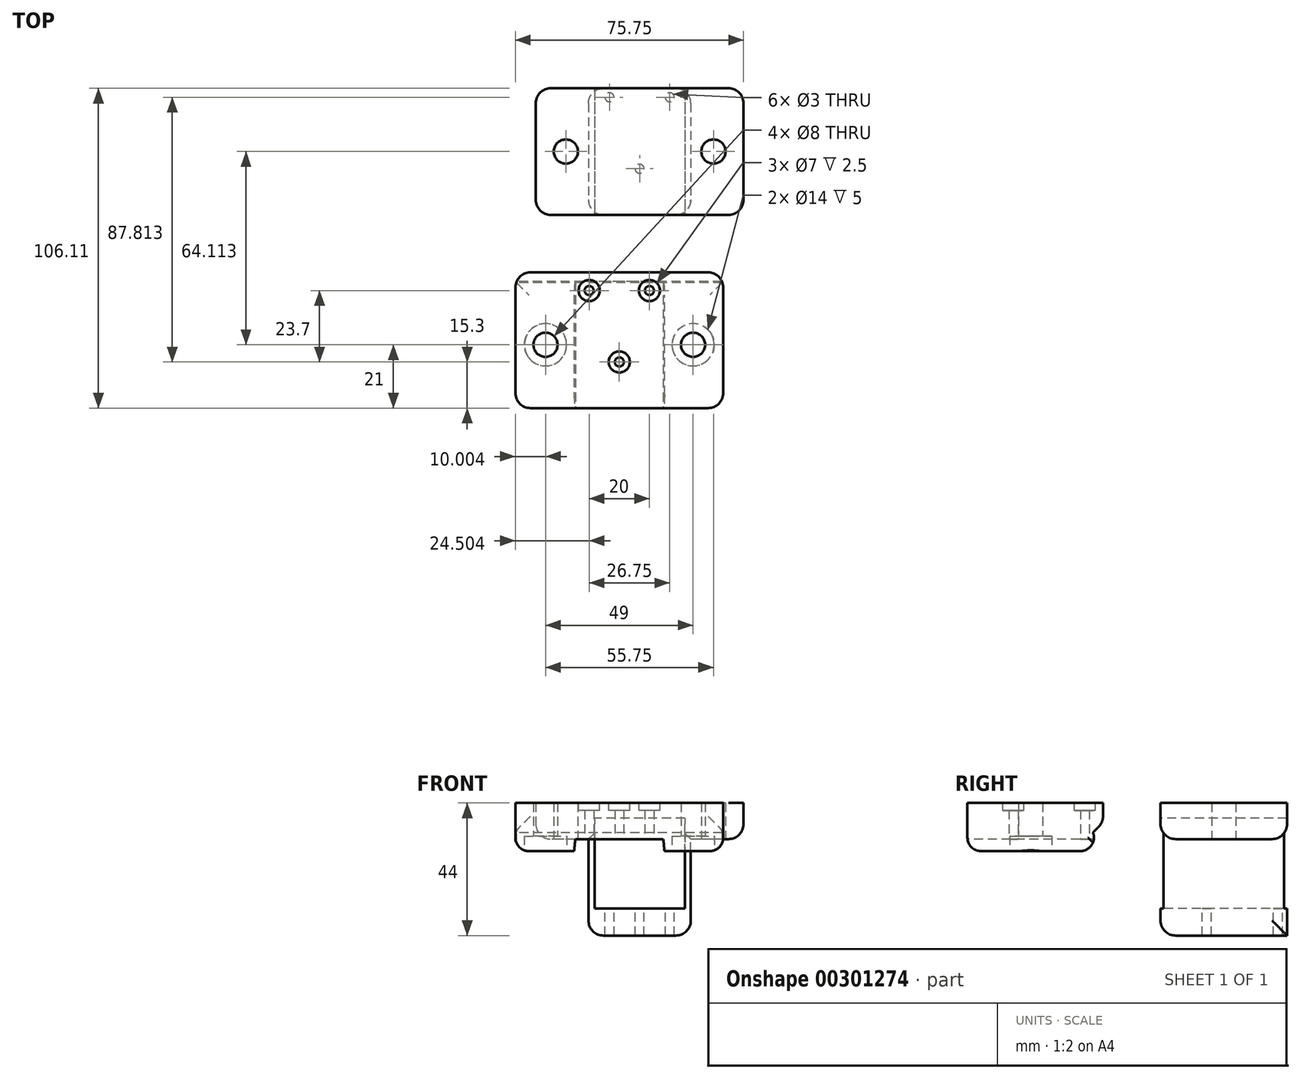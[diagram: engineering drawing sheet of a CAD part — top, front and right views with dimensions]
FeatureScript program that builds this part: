
annotation { "Feature Type Name" : "Feature", "Feature Type Description" : "" }
export const myFeature = defineFeature(function(context is Context, id is Id, definition is map)
    precondition{}
    {
        {
            var Q0;
            Q0=qCreatedBy(makeId("Top.planeOp"),FACE);
            var sketch = newSketch(context, id + "F0", { "sketchPlane" : qUnion([Q0])});
            skLineSegment(sketch, "E0.bottom", {"start": v(-79.38, 0) * mm, "end": v(-10.38, 0) * mm});
            skLineSegment(sketch, "E0.top", {"start": v(-79.38, -42) * mm, "end": v(-10.38, -42) * mm});
            skLineSegment(sketch, "E0.left", {"start": v(-79.38, 0) * mm, "end": v(-79.38, -42) * mm});
            skLineSegment(sketch, "E0.right", {"start": v(-10.38, 0) * mm, "end": v(-10.38, -42) * mm});
            skPoint(sketch, "E1", {"position": v(-59.38, 0) * mm});
            skLineSegment(sketch, "E2", {"start": v(-59.38, 0) * mm, "end": v(-59.38, -42) * mm});
            skPoint(sketch, "E3", {"position": v(-30.38, 0) * mm});
            skLineSegment(sketch, "E4", {"start": v(-30.38, 0) * mm, "end": v(-30.38, -42) * mm});
            skLineSegment(sketch, "E5", {"start": v(-44.88, 0) * mm, "end": v(-44.88, -42) * mm});
            skLineSegment(sketch, "E6", {"start": v(-59.38, -3) * mm, "end": v(-30.38, -3) * mm});
            skPoint(sketch, "E7", {"position": v(-44.88, -3) * mm});
            skPoint(sketch, "E8", {"position": v(-54.88, -3) * mm});
            skPoint(sketch, "E9", {"position": v(-34.88, -3) * mm});
            skPoint(sketch, "E10", {"position": v(-44.88, -26.7) * mm});
            skCircle(sketch, "E11", {"center": v(-54.88, -3) * mm, "radius": 1.5 * mm});
            skCircle(sketch, "E12", {"center": v(-34.88, -3) * mm, "radius": 1.5 * mm});
            skCircle(sketch, "E13", {"center": v(-44.88, -26.7) * mm, "radius": 1.5 * mm});
            skPoint(sketch, "E14", {"position": v(-20.38, -42) * mm});
            skLineSegment(sketch, "E15", {"start": v(-20.38, -42) * mm, "end": v(-20.38, 0) * mm});
            skPoint(sketch, "E16", {"position": v(-20.38, -21) * mm});
            skCircle(sketch, "E17", {"center": v(-20.38, -21) * mm, "radius": 4 * mm});
            skPoint(sketch, "E18", {"position": v(-69.38, -42) * mm});
            skLineSegment(sketch, "E19", {"start": v(-69.38, -42) * mm, "end": v(-69.38, 0) * mm});
            skPoint(sketch, "E20", {"position": v(-69.38, -21) * mm});
            skCircle(sketch, "E21", {"center": v(-69.38, -21) * mm, "radius": 4 * mm});
            skSolve(sketch);
        }
        {
            var Q0;
            {var subQ5=sQuery(id+"F0.wireOp",EDGE,"E0.right");Q0=makeQuery(id+"F0.imprint","IMPRINT",FACE,{"disambiguationData":[TD([[makeQuery(id+"F0.imprint","IMPRINT",EDGE,{"derivedFrom":subQ5}),-1.0]])]});}
            var Q1;
            {var subQ0=sQuery(id+"F0.wireOp",EDGE,"E4");var subQ4=sQuery(id+"F0.wireOp",EDGE,"E0.bottom");var subQ5=makeQuery(id+"F0.imprint","INTERSECT",VERTEX,{"derivedFrom":[subQ4,subQ0]});Q1=makeQuery(id+"F0.imprint","IMPRINT",FACE,{"disambiguationData":[TD([[makeQuery(id+"F0.imprint","IMPRINT",EDGE,{"disambiguationData":[TD([[subQ5,-1.0]])],"derivedFrom":subQ4}),-1.0]])]});}
            var Q2;
            {var subQ1=sQuery(id+"F0.wireOp",EDGE,"E0.top");var subQ5=sQuery(id+"F0.wireOp",EDGE,"E4");var subQ6=makeQuery(id+"F0.imprint","INTERSECT",VERTEX,{"derivedFrom":[subQ1,subQ5]});Q2=makeQuery(id+"F0.imprint","IMPRINT",FACE,{"disambiguationData":[TD([[makeQuery(id+"F0.imprint","IMPRINT",EDGE,{"disambiguationData":[TD([[subQ6,1.0]])],"derivedFrom":subQ1}),1.0]])]});}
            var Q3;
            {var subQ1=sQuery(id+"F0.wireOp",EDGE,"E0.top");var subQ8=sQuery(id+"F0.wireOp",EDGE,"E2");var subQ9=makeQuery(id+"F0.imprint","INTERSECT",VERTEX,{"derivedFrom":[subQ1,subQ8]});Q3=makeQuery(id+"F0.imprint","IMPRINT",FACE,{"disambiguationData":[TD([[makeQuery(id+"F0.imprint","IMPRINT",EDGE,{"disambiguationData":[TD([[subQ9,-1.0]])],"derivedFrom":subQ1}),1.0]])]});}
            var Q4;
            {var subQ0=sQuery(id+"F0.wireOp",EDGE,"E2");var subQ4=sQuery(id+"F0.wireOp",EDGE,"E0.bottom");var subQ5=makeQuery(id+"F0.imprint","INTERSECT",VERTEX,{"derivedFrom":[subQ4,subQ0]});Q4=makeQuery(id+"F0.imprint","IMPRINT",FACE,{"disambiguationData":[TD([[makeQuery(id+"F0.imprint","IMPRINT",EDGE,{"disambiguationData":[TD([[subQ5,1.0]])],"derivedFrom":subQ4}),-1.0]])]});}
            var Q5;
            {var subQ5=sQuery(id+"F0.wireOp",EDGE,"E0.left");Q5=makeQuery(id+"F0.imprint","IMPRINT",FACE,{"disambiguationData":[TD([[makeQuery(id+"F0.imprint","IMPRINT",EDGE,{"derivedFrom":subQ5}),1.0]])]});}
            var Q6;
            {var subQ1=sQuery(id+"F0.wireOp",EDGE,"E0.bottom");var subQ5=sQuery(id+"F0.wireOp",EDGE,"E2");var subQ6=makeQuery(id+"F0.imprint","INTERSECT",VERTEX,{"derivedFrom":[subQ1,subQ5]});Q6=makeQuery(id+"F0.imprint","IMPRINT",FACE,{"disambiguationData":[TD([[makeQuery(id+"F0.imprint","IMPRINT",EDGE,{"disambiguationData":[TD([[subQ6,-1.0]])],"derivedFrom":subQ1}),-1.0]])]});}
            var Q7;
            {var subQ5=sQuery(id+"F0.wireOp",EDGE,"E4");var subQ6=sQuery(id+"F0.wireOp",EDGE,"E0.bottom");var subQ7=makeQuery(id+"F0.imprint","INTERSECT",VERTEX,{"derivedFrom":[subQ6,subQ5]});Q7=makeQuery(id+"F0.imprint","IMPRINT",FACE,{"disambiguationData":[TD([[makeQuery(id+"F0.imprint","IMPRINT",EDGE,{"disambiguationData":[TD([[subQ7,1.0]])],"derivedFrom":subQ6}),-1.0]])]});}
            extrude(context, id + "F1", {"entities" : qUnion([Q0, Q1, Q2, Q3, Q4, Q5, Q6, Q7]), "depth" : 12 * mm});
        }
        {
            var Q0;
            {var subQ5=sQuery(id+"F0.wireOp",EDGE,"E0.right");Q0=makeQuery(id+"F0.imprint","IMPRINT",FACE,{"disambiguationData":[TD([[makeQuery(id+"F0.imprint","IMPRINT",EDGE,{"derivedFrom":subQ5}),-1.0]])]});}
            var Q1;
            {var subQ0=sQuery(id+"F0.wireOp",EDGE,"E4");var subQ4=sQuery(id+"F0.wireOp",EDGE,"E0.bottom");var subQ5=makeQuery(id+"F0.imprint","INTERSECT",VERTEX,{"derivedFrom":[subQ4,subQ0]});Q1=makeQuery(id+"F0.imprint","IMPRINT",FACE,{"disambiguationData":[TD([[makeQuery(id+"F0.imprint","IMPRINT",EDGE,{"disambiguationData":[TD([[subQ5,-1.0]])],"derivedFrom":subQ4}),-1.0]])]});}
            var Q2;
            {var subQ0=sQuery(id+"F0.wireOp",EDGE,"E2");var subQ4=sQuery(id+"F0.wireOp",EDGE,"E0.bottom");var subQ5=makeQuery(id+"F0.imprint","INTERSECT",VERTEX,{"derivedFrom":[subQ4,subQ0]});Q2=makeQuery(id+"F0.imprint","IMPRINT",FACE,{"disambiguationData":[TD([[makeQuery(id+"F0.imprint","IMPRINT",EDGE,{"disambiguationData":[TD([[subQ5,1.0]])],"derivedFrom":subQ4}),-1.0]])]});}
            var Q3;
            {var subQ5=sQuery(id+"F0.wireOp",EDGE,"E0.left");Q3=makeQuery(id+"F0.imprint","IMPRINT",FACE,{"disambiguationData":[TD([[makeQuery(id+"F0.imprint","IMPRINT",EDGE,{"derivedFrom":subQ5}),1.0]])]});}
            extrude(context, id + "F2", {"entities" : qUnion([Q0, Q1, Q2, Q3]), "operationType" : NewBodyOperationType.ADD, "oppositeDirection" : true, "depth" : 4 * mm});
        }
        {
            var Q0;
            Q0=makeQuery(id+"F2.opExtrude","CAP_EDGE",EDGE,{"disambiguationData":[OSD([sQuery(id+"F0.wireOp",EDGE,"E2")])],"isStart":false});
            chamfer(context, id + "F3", {"entities" : qUnion([Q0]), "chamferType" : ChamferType.TWO_OFFSETS, "width1" : 0.5 * mm, "oppositeDirection" : false, "width2" : 5 * mm, "tangentPropagation" : true});
        }
        {
            var Q0;
            Q0=makeQuery(id+"F2.opExtrude","CAP_EDGE",EDGE,{"disambiguationData":[OSD([sQuery(id+"F0.wireOp",EDGE,"E4")])],"isStart":false});
            chamfer(context, id + "F4", {"entities" : qUnion([Q0]), "chamferType" : ChamferType.TWO_OFFSETS, "width1" : 5 * mm, "oppositeDirection" : false, "width2" : 0.5 * mm, "tangentPropagation" : true});
        }
        {
            var Q0;
            Q0=makeQuery(id+"F2.opExtrude","CAP_FACE",FACE,{"disambiguationData":[OSD([sQuery(id+"F0.wireOp",EDGE,"E0.bottom"),sQuery(id+"F0.wireOp",EDGE,"E0.top"),sQuery(id+"F0.wireOp",EDGE,"E0.right"),sQuery(id+"F0.wireOp",EDGE,"E4"),sQuery(id+"F0.wireOp",EDGE,"E17")])],"isStart":false});
            var sketch = newSketch(context, id + "F5", { "sketchPlane" : qUnion([Q0])});
            skCircle(sketch, "E22", {"center": v(-20.38, 21) * mm, "radius": 7 * mm});
            skSolve(sketch);
        }
        {
            var Q0;
            Q0=makeQuery(id+"F5.imprint","IMPRINT",FACE,{"disambiguationData":[TD([[makeQuery(id+"F5.imprint","IMPRINT",EDGE,{"derivedFrom":sQuery(id+"F5.wireOp",EDGE,"E22")}),1.0]])]});
            extrude(context, id + "F6", {"entities" : qUnion([Q0]), "operationType" : NewBodyOperationType.REMOVE, "oppositeDirection" : true, "depth" : 5 * mm});
        }
        {
            var Q0;
            Q0=makeQuery(id+"F2.opExtrude","CAP_FACE",FACE,{"disambiguationData":[OSD([sQuery(id+"F0.wireOp",EDGE,"E0.bottom"),sQuery(id+"F0.wireOp",EDGE,"E0.top"),sQuery(id+"F0.wireOp",EDGE,"E0.left"),sQuery(id+"F0.wireOp",EDGE,"E2"),sQuery(id+"F0.wireOp",EDGE,"E21")])],"isStart":false});
            var sketch = newSketch(context, id + "F7", { "sketchPlane" : qUnion([Q0])});
            skCircle(sketch, "E23", {"center": v(-69.38, 21) * mm, "radius": 7 * mm});
            skSolve(sketch);
        }
        {
            var Q0;
            Q0=makeQuery(id+"F7.imprint","IMPRINT",FACE,{"disambiguationData":[TD([[makeQuery(id+"F7.imprint","IMPRINT",EDGE,{"derivedFrom":sQuery(id+"F7.wireOp",EDGE,"E23")}),1.0]])]});
            extrude(context, id + "F8", {"entities" : qUnion([Q0]), "operationType" : NewBodyOperationType.REMOVE, "oppositeDirection" : true, "depth" : 5 * mm});
        }
        {
            var Q0;
            Q0=makeQuery(id+"F2.opExtrude","CAP_EDGE",EDGE,{"disambiguationData":[OSD([sQuery(id+"F0.wireOp",EDGE,"E0.right")])],"isStart":false});
            var Q1;
            Q1=makeQuery(id+"F2.opExtrude","CAP_EDGE",EDGE,{"disambiguationData":[OSD([sQuery(id+"F0.wireOp",EDGE,"E0.left")])],"isStart":false});
            var Q2;
            {var subQ0=sQuery(id+"F0.wireOp",EDGE,"E0.top");Q2=makeQuery(id+"F2.opExtrude","CAP_EDGE",EDGE,{"disambiguationData":[OSD([subQ0]),TDD([makeQuery(id+"F0.imprint","IMPRINT",EDGE,{"disambiguationData":[TD([[makeQuery(id+"F0.imprint","INTERSECT",VERTEX,{"derivedFrom":[subQ0,sQuery(id+"F0.wireOp",EDGE,"E0.left")]}),-1.0]])],"derivedFrom":subQ0}),makeQuery(id+"F0.imprint","IMPRINT",EDGE,{"disambiguationData":[TD([[makeQuery(id+"F0.imprint","INTERSECT",VERTEX,{"derivedFrom":[subQ0,sQuery(id+"F0.wireOp",EDGE,"E2")]}),1.0]])],"derivedFrom":subQ0})])],"isStart":false});}
            var Q3;
            {var subQ0=sQuery(id+"F0.wireOp",EDGE,"E0.bottom");Q3=makeQuery(id+"F2.opExtrude","CAP_EDGE",EDGE,{"disambiguationData":[OSD([subQ0]),TDD([makeQuery(id+"F0.imprint","IMPRINT",EDGE,{"disambiguationData":[TD([[makeQuery(id+"F0.imprint","INTERSECT",VERTEX,{"derivedFrom":[subQ0,sQuery(id+"F0.wireOp",EDGE,"E0.left")]}),-1.0]])],"derivedFrom":subQ0}),makeQuery(id+"F0.imprint","IMPRINT",EDGE,{"disambiguationData":[TD([[makeQuery(id+"F0.imprint","INTERSECT",VERTEX,{"derivedFrom":[subQ0,sQuery(id+"F0.wireOp",EDGE,"E2")]}),1.0]])],"derivedFrom":subQ0})])],"isStart":false});}
            fillet(context, id + "F9", {"entities" : qUnion([Q0, Q1, Q2, Q3]), "radius" : 4.5 * mm, "allowEdgeOverflow" : false});
        }
        {
            var Q0;
            {var subQ0=sQuery(id+"F0.wireOp",EDGE,"E0.bottom");Q0=makeQuery(id+"F2.boolean.opBoolean","MERGE",FACE,{"derivedFrom":[makeQuery(id+"F1.opExtrude","SWEPT_FACE",FACE,{"disambiguationData":[OSD([subQ0])]}),makeQuery(id+"F2.opExtrude","SWEPT_FACE",FACE,{"disambiguationData":[OSD([subQ0]),TDD([makeQuery(id+"F0.imprint","IMPRINT",EDGE,{"disambiguationData":[TD([[makeQuery(id+"F0.imprint","INTERSECT",VERTEX,{"derivedFrom":[subQ0,sQuery(id+"F0.wireOp",EDGE,"E0.left")]}),-1.0]])],"derivedFrom":subQ0}),makeQuery(id+"F0.imprint","IMPRINT",EDGE,{"disambiguationData":[TD([[makeQuery(id+"F0.imprint","INTERSECT",VERTEX,{"derivedFrom":[subQ0,sQuery(id+"F0.wireOp",EDGE,"E2")]}),1.0]])],"derivedFrom":subQ0})])]}),makeQuery(id+"F2.opExtrude","SWEPT_FACE",FACE,{"disambiguationData":[OSD([subQ0]),TDD([makeQuery(id+"F0.imprint","IMPRINT",EDGE,{"disambiguationData":[TD([[makeQuery(id+"F0.imprint","INTERSECT",VERTEX,{"derivedFrom":[subQ0,sQuery(id+"F0.wireOp",EDGE,"E4")]}),-1.0]])],"derivedFrom":subQ0}),makeQuery(id+"F0.imprint","IMPRINT",EDGE,{"disambiguationData":[TD([[makeQuery(id+"F0.imprint","INTERSECT",VERTEX,{"derivedFrom":[subQ0,sQuery(id+"F0.wireOp",EDGE,"E0.right")]}),1.0]])],"derivedFrom":subQ0})])]})]});}
            extrude(context, id + "F10", {"entities" : qUnion([Q0]), "operationType" : NewBodyOperationType.ADD, "depth" : 3 * mm});
        }
        {
            var Q0;
            {var subQ0=sQuery(id+"F0.wireOp",EDGE,"E0.bottom");var subQ3=makeQuery(id+"F0.imprint","IMPRINT",EDGE,{"disambiguationData":[TD([[makeQuery(id+"F0.imprint","INTERSECT",VERTEX,{"derivedFrom":[subQ0,sQuery(id+"F0.wireOp",EDGE,"E2")]}),1.0]])],"derivedFrom":subQ0});var subQ4=makeQuery(id+"F0.imprint","IMPRINT",EDGE,{"disambiguationData":[TD([[makeQuery(id+"F0.imprint","INTERSECT",VERTEX,{"derivedFrom":[subQ0,sQuery(id+"F0.wireOp",EDGE,"E0.left")]}),-1.0]])],"derivedFrom":subQ0});Q0=makeQuery(id+"F10.opExtrude","CAP_EDGE",EDGE,{"disambiguationData":[OSD([subQ0]),TDD([makeQuery(id+"F9.opFillet","BLEND_EDGE",EDGE,{"blendedFrom":[makeQuery(id+"F2.opExtrude","CAP_EDGE",EDGE,{"disambiguationData":[OSD([subQ0]),TDD([subQ4,subQ3])],"isStart":false}),makeQuery(id+"F2.boolean.opBoolean","MERGE",FACE,{"derivedFrom":[makeQuery(id+"F1.opExtrude","SWEPT_FACE",FACE,{"disambiguationData":[OSD([subQ0])]}),makeQuery(id+"F2.opExtrude","SWEPT_FACE",FACE,{"disambiguationData":[OSD([subQ0]),TDD([subQ4,subQ3])]}),makeQuery(id+"F2.opExtrude","SWEPT_FACE",FACE,{"disambiguationData":[OSD([subQ0]),TDD([makeQuery(id+"F0.imprint","IMPRINT",EDGE,{"disambiguationData":[TD([[makeQuery(id+"F0.imprint","INTERSECT",VERTEX,{"derivedFrom":[subQ0,sQuery(id+"F0.wireOp",EDGE,"E4")]}),-1.0]])],"derivedFrom":subQ0}),makeQuery(id+"F0.imprint","IMPRINT",EDGE,{"disambiguationData":[TD([[makeQuery(id+"F0.imprint","INTERSECT",VERTEX,{"derivedFrom":[subQ0,sQuery(id+"F0.wireOp",EDGE,"E0.right")]}),1.0]])],"derivedFrom":subQ0})])]})]})],"blendedInto":[makeQuery(id+"F2.boolean.opBoolean","MERGE",FACE,{"derivedFrom":[makeQuery(id+"F1.opExtrude","SWEPT_FACE",FACE,{"disambiguationData":[OSD([subQ0])]}),makeQuery(id+"F2.opExtrude","SWEPT_FACE",FACE,{"disambiguationData":[OSD([subQ0]),TDD([subQ4,subQ3])]}),makeQuery(id+"F2.opExtrude","SWEPT_FACE",FACE,{"disambiguationData":[OSD([subQ0]),TDD([makeQuery(id+"F0.imprint","IMPRINT",EDGE,{"disambiguationData":[TD([[makeQuery(id+"F0.imprint","INTERSECT",VERTEX,{"derivedFrom":[subQ0,sQuery(id+"F0.wireOp",EDGE,"E4")]}),-1.0]])],"derivedFrom":subQ0}),makeQuery(id+"F0.imprint","IMPRINT",EDGE,{"disambiguationData":[TD([[makeQuery(id+"F0.imprint","INTERSECT",VERTEX,{"derivedFrom":[subQ0,sQuery(id+"F0.wireOp",EDGE,"E0.right")]}),1.0]])],"derivedFrom":subQ0})])]})]})]})])],"isStart":false});}
            chamfer(context, id + "F11", {"entities" : qUnion([Q0]), "width" : 5 * mm, "tangentPropagation" : true});
        }
        {
            var Q0;
            {var subQ0=sQuery(id+"F0.wireOp",EDGE,"E0.bottom");Q0=makeQuery(id+"F10.boolean.opBoolean","MERGE",FACE,{"derivedFrom":[makeQuery(id+"F1.opExtrude","CAP_FACE",FACE,{"disambiguationData":[OSD([subQ0,sQuery(id+"F0.wireOp",EDGE,"E0.top"),sQuery(id+"F0.wireOp",EDGE,"E0.left"),sQuery(id+"F0.wireOp",EDGE,"E0.right"),sQuery(id+"F0.wireOp",EDGE,"E11"),sQuery(id+"F0.wireOp",EDGE,"E12"),sQuery(id+"F0.wireOp",EDGE,"E13"),sQuery(id+"F0.wireOp",EDGE,"E17"),sQuery(id+"F0.wireOp",EDGE,"E21")])],"isStart":false}),makeQuery(id+"F10.opExtrude","SWEPT_FACE",FACE,{"disambiguationData":[OSD([subQ0]),TDD([makeQuery(id+"F1.opExtrude","CAP_EDGE",EDGE,{"disambiguationData":[OSD([subQ0])],"isStart":false})])]})]});}
            var sketch = newSketch(context, id + "F12", { "sketchPlane" : qUnion([Q0])});
            skCircle(sketch, "E24", {"center": v(-34.88, -3) * mm, "radius": 3.5 * mm});
            skCircle(sketch, "E25", {"center": v(-54.88, -3) * mm, "radius": 3.5 * mm});
            skCircle(sketch, "E26", {"center": v(-44.88, -26.7) * mm, "radius": 3.5 * mm});
            skSolve(sketch);
        }
        {
            var Q0;
            Q0=makeQuery(id+"F12.imprint","IMPRINT",FACE,{"disambiguationData":[TD([[makeQuery(id+"F12.imprint","IMPRINT",EDGE,{"derivedFrom":sQuery(id+"F12.wireOp",EDGE,"E26")}),1.0]])]});
            var Q1;
            Q1=makeQuery(id+"F12.imprint","IMPRINT",FACE,{"disambiguationData":[TD([[makeQuery(id+"F12.imprint","IMPRINT",EDGE,{"derivedFrom":sQuery(id+"F12.wireOp",EDGE,"E24")}),1.0]])]});
            var Q2;
            Q2=makeQuery(id+"F12.imprint","IMPRINT",FACE,{"disambiguationData":[TD([[makeQuery(id+"F12.imprint","IMPRINT",EDGE,{"derivedFrom":sQuery(id+"F12.wireOp",EDGE,"E25")}),1.0]])]});
            extrude(context, id + "F13", {"entities" : qUnion([Q0, Q1, Q2]), "operationType" : NewBodyOperationType.REMOVE, "oppositeDirection" : true, "depth" : 2.5 * mm});
        }
        {
            var Q0;
            Q0=qCreatedBy(makeId("Top.planeOp"),FACE);
            var sketch = newSketch(context, id + "F14", { "sketchPlane" : qUnion([Q0])});
            skLineSegment(sketch, "E27.bottom", {"start": v(-3.63, 64.11) * mm, "end": v(-72.63, 64.11) * mm});
            skLineSegment(sketch, "E27.top", {"start": v(-3.63, 22.11) * mm, "end": v(-72.63, 22.11) * mm});
            skLineSegment(sketch, "E27.left", {"start": v(-3.63, 64.11) * mm, "end": v(-3.63, 22.11) * mm});
            skLineSegment(sketch, "E27.right", {"start": v(-72.63, 64.11) * mm, "end": v(-72.63, 22.11) * mm});
            skPoint(sketch, "E28", {"position": v(-72.63, 43.11) * mm});
            skLineSegment(sketch, "E29", {"start": v(-72.63, 43.11) * mm, "end": v(-3.63, 43.11) * mm});
            skPoint(sketch, "E30", {"position": v(-38.13, 64.11) * mm});
            skLineSegment(sketch, "E31", {"start": v(-38.13, 64.11) * mm, "end": v(-38.13, 22.11) * mm});
            skPoint(sketch, "E32", {"position": v(-23.63, 64.11) * mm});
            skLineSegment(sketch, "E33", {"start": v(-23.63, 64.11) * mm, "end": v(-23.63, 22.11) * mm});
            skPoint(sketch, "E34", {"position": v(-52.63, 64.11) * mm});
            skLineSegment(sketch, "E35", {"start": v(-52.63, 64.11) * mm, "end": v(-52.63, 22.11) * mm});
            skPoint(sketch, "E36", {"position": v(-52.63, 43.11) * mm});
            skPoint(sketch, "E37", {"position": v(-62.63, 43.11) * mm});
            skCircle(sketch, "E38", {"center": v(-62.63, 43.11) * mm, "radius": 4 * mm});
            skPoint(sketch, "E39", {"position": v(-13.63, 43.11) * mm});
            skCircle(sketch, "E40", {"center": v(-13.63, 43.11) * mm, "radius": 4 * mm});
            skLineSegment(sketch, "E41", {"start": v(-55.13, 64.11) * mm, "end": v(-55.13, 22.11) * mm});
            skLineSegment(sketch, "E42", {"start": v(-21.13, 64.11) * mm, "end": v(-21.13, 22.11) * mm});
            skSolve(sketch);
        }
        {
            var Q0;
            {var subQ1=sQuery(id+"F14.wireOp",EDGE,"E27.left");var subQ5=sQuery(id+"F14.wireOp",EDGE,"E27.bottom");var subQ6=makeQuery(id+"F14.imprint","INTERSECT",VERTEX,{"derivedFrom":[subQ5,subQ1]});Q0=makeQuery(id+"F14.imprint","IMPRINT",FACE,{"disambiguationData":[TD([[makeQuery(id+"F14.imprint","IMPRINT",EDGE,{"disambiguationData":[TD([[subQ6,-1.0]])],"derivedFrom":subQ5}),1.0]])]});}
            var Q1;
            {var subQ0=sQuery(id+"F14.wireOp",EDGE,"E31");var subQ1=sQuery(id+"F14.wireOp",EDGE,"E27.bottom");var subQ2=makeQuery(id+"F14.imprint","INTERSECT",VERTEX,{"derivedFrom":[subQ1,subQ0]});Q1=makeQuery(id+"F14.imprint","IMPRINT",FACE,{"disambiguationData":[TD([[makeQuery(id+"F14.imprint","IMPRINT",EDGE,{"disambiguationData":[TD([[subQ2,1.0]])],"derivedFrom":subQ1}),1.0]])]});}
            var Q2;
            {var subQ0=sQuery(id+"F14.wireOp",EDGE,"E31");var subQ1=sQuery(id+"F14.wireOp",EDGE,"E27.bottom");var subQ2=makeQuery(id+"F14.imprint","INTERSECT",VERTEX,{"derivedFrom":[subQ1,subQ0]});Q2=makeQuery(id+"F14.imprint","IMPRINT",FACE,{"disambiguationData":[TD([[makeQuery(id+"F14.imprint","IMPRINT",EDGE,{"disambiguationData":[TD([[subQ2,-1.0]])],"derivedFrom":subQ1}),1.0]])]});}
            var Q3;
            {var subQ5=sQuery(id+"F14.wireOp",EDGE,"E27.left");var subQ8=sQuery(id+"F14.wireOp",EDGE,"E27.top");var subQ9=makeQuery(id+"F14.imprint","INTERSECT",VERTEX,{"derivedFrom":[subQ8,subQ5]});Q3=makeQuery(id+"F14.imprint","IMPRINT",FACE,{"disambiguationData":[TD([[makeQuery(id+"F14.imprint","IMPRINT",EDGE,{"disambiguationData":[TD([[subQ9,-1.0]])],"derivedFrom":subQ8}),-1.0]])]});}
            var Q4;
            {var subQ0=sQuery(id+"F14.wireOp",EDGE,"E31");var subQ1=sQuery(id+"F14.wireOp",EDGE,"E27.top");var subQ2=makeQuery(id+"F14.imprint","INTERSECT",VERTEX,{"derivedFrom":[subQ1,subQ0]});Q4=makeQuery(id+"F14.imprint","IMPRINT",FACE,{"disambiguationData":[TD([[makeQuery(id+"F14.imprint","IMPRINT",EDGE,{"disambiguationData":[TD([[subQ2,1.0]])],"derivedFrom":subQ1}),-1.0]])]});}
            var Q5;
            {var subQ0=sQuery(id+"F14.wireOp",EDGE,"E31");var subQ1=sQuery(id+"F14.wireOp",EDGE,"E27.top");var subQ2=makeQuery(id+"F14.imprint","INTERSECT",VERTEX,{"derivedFrom":[subQ1,subQ0]});Q5=makeQuery(id+"F14.imprint","IMPRINT",FACE,{"disambiguationData":[TD([[makeQuery(id+"F14.imprint","IMPRINT",EDGE,{"disambiguationData":[TD([[subQ2,-1.0]])],"derivedFrom":subQ1}),-1.0]])]});}
            var Q6;
            {var subQ5=sQuery(id+"F14.wireOp",EDGE,"E27.top");var subQ7=sQuery(id+"F14.wireOp",EDGE,"E27.right");var subQ8=makeQuery(id+"F14.imprint","INTERSECT",VERTEX,{"derivedFrom":[subQ5,subQ7]});Q6=makeQuery(id+"F14.imprint","IMPRINT",FACE,{"disambiguationData":[TD([[makeQuery(id+"F14.imprint","IMPRINT",EDGE,{"disambiguationData":[TD([[subQ8,1.0]])],"derivedFrom":subQ5}),-1.0]])]});}
            var Q7;
            {var subQ5=sQuery(id+"F14.wireOp",EDGE,"E27.right");var subQ6=sQuery(id+"F14.wireOp",EDGE,"E27.bottom");var subQ7=makeQuery(id+"F14.imprint","INTERSECT",VERTEX,{"derivedFrom":[subQ6,subQ5]});Q7=makeQuery(id+"F14.imprint","IMPRINT",FACE,{"disambiguationData":[TD([[makeQuery(id+"F14.imprint","IMPRINT",EDGE,{"disambiguationData":[TD([[subQ7,1.0]])],"derivedFrom":subQ6}),1.0]])]});}
            var Q8;
            {var subQ0=sQuery(id+"F14.wireOp",EDGE,"E35");var subQ1=sQuery(id+"F14.wireOp",EDGE,"E27.bottom");var subQ2=makeQuery(id+"F14.imprint","INTERSECT",VERTEX,{"derivedFrom":[subQ1,subQ0]});Q8=makeQuery(id+"F14.imprint","IMPRINT",FACE,{"disambiguationData":[TD([[makeQuery(id+"F14.imprint","IMPRINT",EDGE,{"disambiguationData":[TD([[subQ2,-1.0]])],"derivedFrom":subQ1}),1.0]])]});}
            var Q9;
            {var subQ0=sQuery(id+"F14.wireOp",EDGE,"E35");var subQ1=sQuery(id+"F14.wireOp",EDGE,"E27.top");var subQ2=makeQuery(id+"F14.imprint","INTERSECT",VERTEX,{"derivedFrom":[subQ1,subQ0]});Q9=makeQuery(id+"F14.imprint","IMPRINT",FACE,{"disambiguationData":[TD([[makeQuery(id+"F14.imprint","IMPRINT",EDGE,{"disambiguationData":[TD([[subQ2,-1.0]])],"derivedFrom":subQ1}),-1.0]])]});}
            var Q10;
            {var subQ0=sQuery(id+"F14.wireOp",EDGE,"E33");var subQ1=sQuery(id+"F14.wireOp",EDGE,"E27.bottom");var subQ2=makeQuery(id+"F14.imprint","INTERSECT",VERTEX,{"derivedFrom":[subQ1,subQ0]});Q10=makeQuery(id+"F14.imprint","IMPRINT",FACE,{"disambiguationData":[TD([[makeQuery(id+"F14.imprint","IMPRINT",EDGE,{"disambiguationData":[TD([[subQ2,1.0]])],"derivedFrom":subQ1}),1.0]])]});}
            var Q11;
            {var subQ0=sQuery(id+"F14.wireOp",EDGE,"E33");var subQ1=sQuery(id+"F14.wireOp",EDGE,"E27.top");var subQ2=makeQuery(id+"F14.imprint","INTERSECT",VERTEX,{"derivedFrom":[subQ1,subQ0]});Q11=makeQuery(id+"F14.imprint","IMPRINT",FACE,{"disambiguationData":[TD([[makeQuery(id+"F14.imprint","IMPRINT",EDGE,{"disambiguationData":[TD([[subQ2,1.0]])],"derivedFrom":subQ1}),-1.0]])]});}
            extrude(context, id + "F15", {"entities" : qUnion([Q0, Q1, Q2, Q3, Q4, Q5, Q6, Q7, Q8, Q9, Q10, Q11]), "depth" : 12 * mm});
        }
        {
            var Q0;
            {var subQ0=sQuery(id+"F14.wireOp",EDGE,"E31");var subQ1=sQuery(id+"F14.wireOp",EDGE,"E27.bottom");var subQ2=makeQuery(id+"F14.imprint","INTERSECT",VERTEX,{"derivedFrom":[subQ1,subQ0]});Q0=makeQuery(id+"F14.imprint","IMPRINT",FACE,{"disambiguationData":[TD([[makeQuery(id+"F14.imprint","IMPRINT",EDGE,{"disambiguationData":[TD([[subQ2,-1.0]])],"derivedFrom":subQ1}),1.0]])]});}
            var Q1;
            {var subQ0=sQuery(id+"F14.wireOp",EDGE,"E31");var subQ1=sQuery(id+"F14.wireOp",EDGE,"E27.top");var subQ2=makeQuery(id+"F14.imprint","INTERSECT",VERTEX,{"derivedFrom":[subQ1,subQ0]});Q1=makeQuery(id+"F14.imprint","IMPRINT",FACE,{"disambiguationData":[TD([[makeQuery(id+"F14.imprint","IMPRINT",EDGE,{"disambiguationData":[TD([[subQ2,-1.0]])],"derivedFrom":subQ1}),-1.0]])]});}
            var Q2;
            {var subQ0=sQuery(id+"F14.wireOp",EDGE,"E31");var subQ1=sQuery(id+"F14.wireOp",EDGE,"E27.top");var subQ2=makeQuery(id+"F14.imprint","INTERSECT",VERTEX,{"derivedFrom":[subQ1,subQ0]});Q2=makeQuery(id+"F14.imprint","IMPRINT",FACE,{"disambiguationData":[TD([[makeQuery(id+"F14.imprint","IMPRINT",EDGE,{"disambiguationData":[TD([[subQ2,1.0]])],"derivedFrom":subQ1}),-1.0]])]});}
            var Q3;
            {var subQ0=sQuery(id+"F14.wireOp",EDGE,"E31");var subQ1=sQuery(id+"F14.wireOp",EDGE,"E27.bottom");var subQ2=makeQuery(id+"F14.imprint","INTERSECT",VERTEX,{"derivedFrom":[subQ1,subQ0]});Q3=makeQuery(id+"F14.imprint","IMPRINT",FACE,{"disambiguationData":[TD([[makeQuery(id+"F14.imprint","IMPRINT",EDGE,{"disambiguationData":[TD([[subQ2,1.0]])],"derivedFrom":subQ1}),1.0]])]});}
            extrude(context, id + "F16", {"entities" : qUnion([Q0, Q1, Q2, Q3]), "operationType" : NewBodyOperationType.REMOVE, "depth" : 7 * mm});
        }
        {
            var Q0;
            {var subQ0=sQuery(id+"F14.wireOp",EDGE,"E35");var subQ1=sQuery(id+"F14.wireOp",EDGE,"E27.bottom");var subQ2=makeQuery(id+"F14.imprint","INTERSECT",VERTEX,{"derivedFrom":[subQ1,subQ0]});Q0=makeQuery(id+"F14.imprint","IMPRINT",FACE,{"disambiguationData":[TD([[makeQuery(id+"F14.imprint","IMPRINT",EDGE,{"disambiguationData":[TD([[subQ2,-1.0]])],"derivedFrom":subQ1}),1.0]])]});}
            var Q1;
            {var subQ0=sQuery(id+"F14.wireOp",EDGE,"E35");var subQ1=sQuery(id+"F14.wireOp",EDGE,"E27.top");var subQ2=makeQuery(id+"F14.imprint","INTERSECT",VERTEX,{"derivedFrom":[subQ1,subQ0]});Q1=makeQuery(id+"F14.imprint","IMPRINT",FACE,{"disambiguationData":[TD([[makeQuery(id+"F14.imprint","IMPRINT",EDGE,{"disambiguationData":[TD([[subQ2,-1.0]])],"derivedFrom":subQ1}),-1.0]])]});}
            var Q2;
            {var subQ0=sQuery(id+"F14.wireOp",EDGE,"E33");var subQ1=sQuery(id+"F14.wireOp",EDGE,"E27.top");var subQ2=makeQuery(id+"F14.imprint","INTERSECT",VERTEX,{"derivedFrom":[subQ1,subQ0]});Q2=makeQuery(id+"F14.imprint","IMPRINT",FACE,{"disambiguationData":[TD([[makeQuery(id+"F14.imprint","IMPRINT",EDGE,{"disambiguationData":[TD([[subQ2,1.0]])],"derivedFrom":subQ1}),-1.0]])]});}
            var Q3;
            {var subQ0=sQuery(id+"F14.wireOp",EDGE,"E33");var subQ1=sQuery(id+"F14.wireOp",EDGE,"E27.bottom");var subQ2=makeQuery(id+"F14.imprint","INTERSECT",VERTEX,{"derivedFrom":[subQ1,subQ0]});Q3=makeQuery(id+"F14.imprint","IMPRINT",FACE,{"disambiguationData":[TD([[makeQuery(id+"F14.imprint","IMPRINT",EDGE,{"disambiguationData":[TD([[subQ2,1.0]])],"derivedFrom":subQ1}),1.0]])]});}
            extrude(context, id + "F17", {"entities" : qUnion([Q0, Q1, Q2, Q3]), "operationType" : NewBodyOperationType.ADD, "oppositeDirection" : true, "depth" : 23 * mm});
        }
        {
            var Q0;
            Q0=makeQuery(id+"F17.opExtrude","CAP_FACE",FACE,{"disambiguationData":[OSD([sQuery(id+"F14.wireOp",EDGE,"E27.bottom"),sQuery(id+"F14.wireOp",EDGE,"E27.top"),sQuery(id+"F14.wireOp",EDGE,"E35"),sQuery(id+"F14.wireOp",EDGE,"E41")])],"isStart":false});
            var sketch = newSketch(context, id + "F18", { "sketchPlane" : qUnion([Q0])});
            skLineSegment(sketch, "E43", {"start": v(-55.13, -64.11) * mm, "end": v(-21.13, -64.11) * mm});
            skLineSegment(sketch, "E44", {"start": v(-55.13, -22.11) * mm, "end": v(-21.13, -22.11) * mm});
            skLineSegment(sketch, "E45", {"start": v(-55.13, -64.11) * mm, "end": v(-55.13, -22.11) * mm});
            skLineSegment(sketch, "E46", {"start": v(-52.63, -64.11) * mm, "end": v(-52.63, -22.11) * mm});
            skLineSegment(sketch, "E47", {"start": v(-21.13, -64.11) * mm, "end": v(-21.13, -22.11) * mm});
            skLineSegment(sketch, "E48", {"start": v(-23.63, -64.11) * mm, "end": v(-23.63, -22.11) * mm});
            skLineSegment(sketch, "E49", {"start": v(-38.13, -22.11) * mm, "end": v(-38.13, -64.11) * mm});
            skLineSegment(sketch, "E50", {"start": v(-52.63, -61.11) * mm, "end": v(-23.63, -61.11) * mm});
            skPoint(sketch, "E51", {"position": v(-38.13, -61.11) * mm});
            skCircle(sketch, "E52", {"center": v(-48.13, -61.11) * mm, "radius": 1.5 * mm});
            skCircle(sketch, "E53", {"center": v(-28.13, -61.11) * mm, "radius": 1.5 * mm});
            skLineSegment(sketch, "E54", {"start": v(-52.63, -37.41) * mm, "end": v(-23.63, -37.41) * mm});
            skCircle(sketch, "E55", {"center": v(-38.13, -37.41) * mm, "radius": 1.5 * mm});
            skSolve(sketch);
        }
        {
            var Q0;
            Q0 = qSketchRegion(id + "F18", true);
            var Q1;
            {var subQ0=sQuery(id+"F18.wireOp",EDGE,"E50");var subQ5=sQuery(id+"F18.wireOp",EDGE,"E46");var subQ6=makeQuery(id+"F18.imprint","INTERSECT",VERTEX,{"derivedFrom":[subQ5,subQ0]});Q1=makeQuery(id+"F18.imprint","IMPRINT",FACE,{"disambiguationData":[TD([[makeQuery(id+"F18.imprint","IMPRINT",EDGE,{"disambiguationData":[TD([[subQ6,-1.0]])],"derivedFrom":subQ5}),-1.0]])]});}
            var Q2;
            {var subQ0=sQuery(id+"F18.wireOp",EDGE,"E50");var subQ1=sQuery(id+"F18.wireOp",EDGE,"E48");var subQ2=makeQuery(id+"F18.imprint","INTERSECT",VERTEX,{"derivedFrom":[subQ1,subQ0]});Q2=makeQuery(id+"F18.imprint","IMPRINT",FACE,{"disambiguationData":[TD([[makeQuery(id+"F18.imprint","IMPRINT",EDGE,{"disambiguationData":[TD([[subQ2,-1.0]])],"derivedFrom":subQ1}),1.0]])]});}
            extrude(context, id + "F19", {"entities" : qUnion([Q0, Q1, Q2]), "operationType" : NewBodyOperationType.ADD, "depth" : 9 * mm});
        }
        {
            var Q0;
            {var subQ0=sQuery(id+"F14.wireOp",EDGE,"E27.right");var subQ1=sQuery(id+"F14.wireOp",EDGE,"E27.top");Q0=makeQuery(id+"F16.boolean.opBoolean","SPLIT",EDGE,{"disambiguationData":[TD([makeQuery(id+"F15.opExtrude","SWEPT_FACE",FACE,{"disambiguationData":[OSD([subQ0])]})])],"derivedFrom":makeQuery(id+"F15.opExtrude","CAP_EDGE",EDGE,{"disambiguationData":[OSD([subQ1])],"isStart":true})});}
            var Q1;
            {var subQ0=sQuery(id+"F14.wireOp",EDGE,"E27.bottom");var subQ1=sQuery(id+"F14.wireOp",EDGE,"E27.right");Q1=makeQuery(id+"F16.boolean.opBoolean","SPLIT",EDGE,{"disambiguationData":[TD([makeQuery(id+"F15.opExtrude","SWEPT_FACE",FACE,{"disambiguationData":[OSD([subQ1])]})])],"derivedFrom":makeQuery(id+"F15.opExtrude","CAP_EDGE",EDGE,{"disambiguationData":[OSD([subQ0])],"isStart":true})});}
            var Q2;
            Q2=makeQuery(id+"F15.opExtrude","CAP_EDGE",EDGE,{"disambiguationData":[OSD([sQuery(id+"F14.wireOp",EDGE,"E27.right")])],"isStart":true});
            fillet(context, id + "F20", {"entities" : qUnion([Q0, Q1, Q2]), "radius" : 5 * mm, "tangentPropagation" : true, "allowEdgeOverflow" : false});
        }
        {
            var Q0;
            {var subQ0=sQuery(id+"F14.wireOp",EDGE,"E27.bottom");var subQ1=sQuery(id+"F14.wireOp",EDGE,"E27.left");Q0=makeQuery(id+"F16.boolean.opBoolean","SPLIT",EDGE,{"disambiguationData":[TD([makeQuery(id+"F15.opExtrude","SWEPT_FACE",FACE,{"disambiguationData":[OSD([subQ1])]})])],"derivedFrom":makeQuery(id+"F15.opExtrude","CAP_EDGE",EDGE,{"disambiguationData":[OSD([subQ0])],"isStart":true})});}
            var Q1;
            Q1=makeQuery(id+"F15.opExtrude","CAP_EDGE",EDGE,{"disambiguationData":[OSD([sQuery(id+"F14.wireOp",EDGE,"E27.left")])],"isStart":true});
            var Q2;
            {var subQ0=sQuery(id+"F14.wireOp",EDGE,"E27.left");var subQ1=sQuery(id+"F14.wireOp",EDGE,"E27.top");Q2=makeQuery(id+"F16.boolean.opBoolean","SPLIT",EDGE,{"disambiguationData":[TD([makeQuery(id+"F15.opExtrude","SWEPT_FACE",FACE,{"disambiguationData":[OSD([subQ0])]})])],"derivedFrom":makeQuery(id+"F15.opExtrude","CAP_EDGE",EDGE,{"disambiguationData":[OSD([subQ1])],"isStart":true})});}
            fillet(context, id + "F21", {"entities" : qUnion([Q0, Q1, Q2]), "radius" : 5 * mm, "tangentPropagation" : true, "allowEdgeOverflow" : false});
        }
        {
            var Q0;
            Q0=makeQuery(id+"F19.opExtrude","CAP_EDGE",EDGE,{"disambiguationData":[OSD([sQuery(id+"F18.wireOp",EDGE,"E47")])],"isStart":false});
            var Q1;
            Q1=makeQuery(id+"F19.opExtrude","CAP_EDGE",EDGE,{"disambiguationData":[OSD([sQuery(id+"F18.wireOp",EDGE,"E44")])],"isStart":false});
            var Q2;
            Q2=makeQuery(id+"F19.opExtrude","CAP_EDGE",EDGE,{"disambiguationData":[OSD([sQuery(id+"F18.wireOp",EDGE,"E45")])],"isStart":false});
            var Q3;
            Q3=makeQuery(id+"F15.opExtrude","SWEPT_EDGE",EDGE,{"disambiguationData":[OSD([sQuery(id+"F14.wireOp",EDGE,"E27.top"),sQuery(id+"F14.wireOp",EDGE,"E27.right")])]});
            var Q4;
            Q4=makeQuery(id+"F15.opExtrude","SWEPT_EDGE",EDGE,{"disambiguationData":[OSD([sQuery(id+"F14.wireOp",EDGE,"E27.top"),sQuery(id+"F14.wireOp",EDGE,"E27.left")])]});
            var Q5;
            Q5=makeQuery(id+"F15.opExtrude","SWEPT_EDGE",EDGE,{"disambiguationData":[OSD([sQuery(id+"F14.wireOp",EDGE,"E27.bottom"),sQuery(id+"F14.wireOp",EDGE,"E27.left")])]});
            var Q6;
            Q6=makeQuery(id+"F15.opExtrude","SWEPT_EDGE",EDGE,{"disambiguationData":[OSD([sQuery(id+"F14.wireOp",EDGE,"E27.bottom"),sQuery(id+"F14.wireOp",EDGE,"E27.right")])]});
            var Q7;
            Q7=makeQuery(id+"F19.boolean.opBoolean","MERGE",EDGE,{"derivedFrom":[makeQuery(id+"F17.opExtrude","SWEPT_EDGE",EDGE,{"disambiguationData":[OSD([sQuery(id+"F14.wireOp",EDGE,"E27.bottom"),sQuery(id+"F14.wireOp",EDGE,"E41")])]}),makeQuery(id+"F19.opExtrude","SWEPT_EDGE",EDGE,{"disambiguationData":[OSD([sQuery(id+"F18.wireOp",EDGE,"E43"),sQuery(id+"F18.wireOp",EDGE,"E45")])]})]});
            var Q8;
            Q8=makeQuery(id+"F19.boolean.opBoolean","MERGE",EDGE,{"derivedFrom":[makeQuery(id+"F17.opExtrude","SWEPT_EDGE",EDGE,{"disambiguationData":[OSD([sQuery(id+"F14.wireOp",EDGE,"E27.bottom"),sQuery(id+"F14.wireOp",EDGE,"E42")])]}),makeQuery(id+"F19.opExtrude","SWEPT_EDGE",EDGE,{"disambiguationData":[OSD([sQuery(id+"F18.wireOp",EDGE,"E43"),sQuery(id+"F18.wireOp",EDGE,"E47")])]})]});
            var Q9;
            Q9=makeQuery(id+"F19.boolean.opBoolean","MERGE",EDGE,{"derivedFrom":[makeQuery(id+"F17.opExtrude","SWEPT_EDGE",EDGE,{"disambiguationData":[OSD([sQuery(id+"F14.wireOp",EDGE,"E27.top"),sQuery(id+"F14.wireOp",EDGE,"E42")])]}),makeQuery(id+"F19.opExtrude","SWEPT_EDGE",EDGE,{"disambiguationData":[OSD([sQuery(id+"F18.wireOp",EDGE,"E44"),sQuery(id+"F18.wireOp",EDGE,"E47")])]})]});
            var Q10;
            Q10=makeQuery(id+"F19.boolean.opBoolean","MERGE",EDGE,{"derivedFrom":[makeQuery(id+"F17.opExtrude","SWEPT_EDGE",EDGE,{"disambiguationData":[OSD([sQuery(id+"F14.wireOp",EDGE,"E27.top"),sQuery(id+"F14.wireOp",EDGE,"E41")])]}),makeQuery(id+"F19.opExtrude","SWEPT_EDGE",EDGE,{"disambiguationData":[OSD([sQuery(id+"F18.wireOp",EDGE,"E44"),sQuery(id+"F18.wireOp",EDGE,"E45")])]})]});
            fillet(context, id + "F22", {"entities" : qUnion([Q0, Q1, Q2, Q3, Q4, Q5, Q6, Q7, Q8, Q9, Q10]), "radius" : 5 * mm, "tangentPropagation" : true, "allowEdgeOverflow" : false});
        }
        {
            var Q0;
            Q0=makeQuery(id+"F10.opExtrude","CAP_EDGE",EDGE,{"disambiguationData":[OSD([sQuery(id+"F0.wireOp",EDGE,"E0.bottom"),sQuery(id+"F0.wireOp",EDGE,"E0.right")])],"isStart":false});
            var Q1;
            {var subQ0=sQuery(id+"F0.wireOp",EDGE,"E0.bottom");var subQ3=makeQuery(id+"F0.imprint","IMPRINT",EDGE,{"disambiguationData":[TD([[makeQuery(id+"F0.imprint","INTERSECT",VERTEX,{"derivedFrom":[subQ0,sQuery(id+"F0.wireOp",EDGE,"E2")]}),1.0]])],"derivedFrom":subQ0});var subQ4=makeQuery(id+"F0.imprint","IMPRINT",EDGE,{"disambiguationData":[TD([[makeQuery(id+"F0.imprint","INTERSECT",VERTEX,{"derivedFrom":[subQ0,sQuery(id+"F0.wireOp",EDGE,"E0.left")]}),-1.0]])],"derivedFrom":subQ0});Q1=makeQuery(id+"F11.opChamfer","BLEND_EDGE",EDGE,{"blendedFrom":[makeQuery(id+"F10.opExtrude","CAP_EDGE",EDGE,{"disambiguationData":[OSD([subQ0]),TDD([makeQuery(id+"F9.opFillet","BLEND_EDGE",EDGE,{"blendedFrom":[makeQuery(id+"F2.opExtrude","CAP_EDGE",EDGE,{"disambiguationData":[OSD([subQ0]),TDD([subQ4,subQ3])],"isStart":false}),makeQuery(id+"F2.boolean.opBoolean","MERGE",FACE,{"derivedFrom":[makeQuery(id+"F1.opExtrude","SWEPT_FACE",FACE,{"disambiguationData":[OSD([subQ0])]}),makeQuery(id+"F2.opExtrude","SWEPT_FACE",FACE,{"disambiguationData":[OSD([subQ0]),TDD([subQ4,subQ3])]}),makeQuery(id+"F2.opExtrude","SWEPT_FACE",FACE,{"disambiguationData":[OSD([subQ0]),TDD([makeQuery(id+"F0.imprint","IMPRINT",EDGE,{"disambiguationData":[TD([[makeQuery(id+"F0.imprint","INTERSECT",VERTEX,{"derivedFrom":[subQ0,sQuery(id+"F0.wireOp",EDGE,"E4")]}),-1.0]])],"derivedFrom":subQ0}),makeQuery(id+"F0.imprint","IMPRINT",EDGE,{"disambiguationData":[TD([[makeQuery(id+"F0.imprint","INTERSECT",VERTEX,{"derivedFrom":[subQ0,sQuery(id+"F0.wireOp",EDGE,"E0.right")]}),1.0]])],"derivedFrom":subQ0})])]})]})],"blendedInto":[makeQuery(id+"F2.boolean.opBoolean","MERGE",FACE,{"derivedFrom":[makeQuery(id+"F1.opExtrude","SWEPT_FACE",FACE,{"disambiguationData":[OSD([subQ0])]}),makeQuery(id+"F2.opExtrude","SWEPT_FACE",FACE,{"disambiguationData":[OSD([subQ0]),TDD([subQ4,subQ3])]}),makeQuery(id+"F2.opExtrude","SWEPT_FACE",FACE,{"disambiguationData":[OSD([subQ0]),TDD([makeQuery(id+"F0.imprint","IMPRINT",EDGE,{"disambiguationData":[TD([[makeQuery(id+"F0.imprint","INTERSECT",VERTEX,{"derivedFrom":[subQ0,sQuery(id+"F0.wireOp",EDGE,"E4")]}),-1.0]])],"derivedFrom":subQ0}),makeQuery(id+"F0.imprint","IMPRINT",EDGE,{"disambiguationData":[TD([[makeQuery(id+"F0.imprint","INTERSECT",VERTEX,{"derivedFrom":[subQ0,sQuery(id+"F0.wireOp",EDGE,"E0.right")]}),1.0]])],"derivedFrom":subQ0})])]})]})]})])],"isStart":false}),makeQuery(id+"F10.opExtrude","CAP_FACE",FACE,{"disambiguationData":[OSD([subQ0])],"isStart":false})],"blendedInto":[makeQuery(id+"F10.opExtrude","CAP_FACE",FACE,{"disambiguationData":[OSD([subQ0])],"isStart":false})]});}
            var Q2;
            Q2=makeQuery(id+"F10.opExtrude","CAP_EDGE",EDGE,{"disambiguationData":[OSD([sQuery(id+"F0.wireOp",EDGE,"E0.bottom"),sQuery(id+"F0.wireOp",EDGE,"E0.left")])],"isStart":false});
            var Q3;
            {var subQ0=sQuery(id+"F0.wireOp",EDGE,"E0.left");var subQ1=sQuery(id+"F0.wireOp",EDGE,"E0.top");Q3=makeQuery(id+"F2.boolean.opBoolean","MERGE",EDGE,{"derivedFrom":[makeQuery(id+"F1.opExtrude","SWEPT_EDGE",EDGE,{"disambiguationData":[OSD([subQ1,subQ0])]}),makeQuery(id+"F2.opExtrude","SWEPT_EDGE",EDGE,{"disambiguationData":[OSD([subQ1,subQ0])]})]});}
            var Q4;
            {var subQ0=sQuery(id+"F0.wireOp",EDGE,"E0.right");var subQ1=sQuery(id+"F0.wireOp",EDGE,"E0.top");Q4=makeQuery(id+"F2.boolean.opBoolean","MERGE",EDGE,{"derivedFrom":[makeQuery(id+"F1.opExtrude","SWEPT_EDGE",EDGE,{"disambiguationData":[OSD([subQ1,subQ0])]}),makeQuery(id+"F2.opExtrude","SWEPT_EDGE",EDGE,{"disambiguationData":[OSD([subQ1,subQ0])]})]});}
            fillet(context, id + "F23", {"entities" : qUnion([Q0, Q1, Q2, Q3, Q4]), "radius" : 5 * mm, "tangentPropagation" : true, "allowEdgeOverflow" : false});
        }
        {
            var Q0;
            {var subQ0=sQuery(id+"F14.wireOp",EDGE,"E35");Q0=makeQuery(id+"F17.boolean.opBoolean","MERGE",FACE,{"derivedFrom":[makeQuery(id+"F16.boolean.opBoolean","COPY",FACE,{"derivedFrom":makeQuery(id+"F16.opExtrude","SWEPT_FACE",FACE,{"disambiguationData":[OSD([subQ0])]})}),makeQuery(id+"F17.opExtrude","SWEPT_FACE",FACE,{"disambiguationData":[OSD([subQ0])]})]});}
            extrude(context, id + "F24", {"entities" : qUnion([Q0]), "operationType" : NewBodyOperationType.REMOVE, "oppositeDirection" : true, "depth" : 0.5 * mm});
        }
        {
            var Q0;
            {var subQ0=sQuery(id+"F14.wireOp",EDGE,"E33");Q0=makeQuery(id+"F17.boolean.opBoolean","MERGE",FACE,{"derivedFrom":[makeQuery(id+"F16.boolean.opBoolean","COPY",FACE,{"derivedFrom":makeQuery(id+"F16.opExtrude","SWEPT_FACE",FACE,{"disambiguationData":[OSD([subQ0])]})}),makeQuery(id+"F17.opExtrude","SWEPT_FACE",FACE,{"disambiguationData":[OSD([subQ0])]})]});}
            extrude(context, id + "F25", {"entities" : qUnion([Q0]), "operationType" : NewBodyOperationType.REMOVE, "oppositeDirection" : true, "depth" : 0.5 * mm});
        }
    });
